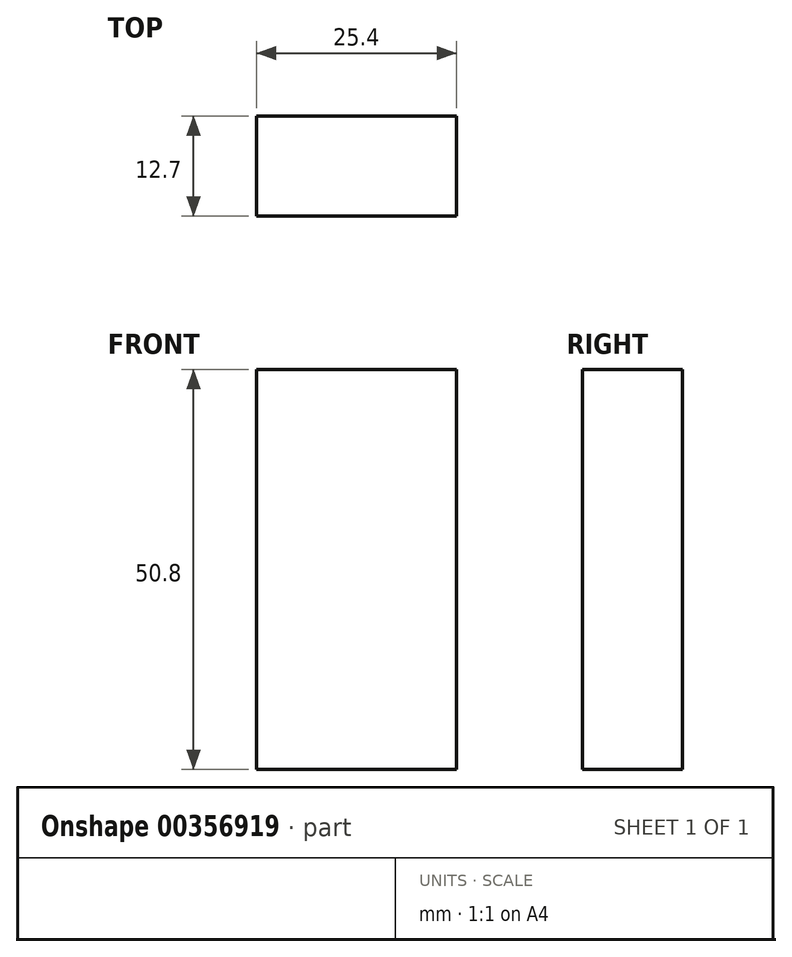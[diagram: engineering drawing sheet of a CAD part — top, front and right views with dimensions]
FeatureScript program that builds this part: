
annotation { "Feature Type Name" : "Feature", "Feature Type Description" : "" }
export const myFeature = defineFeature(function(context is Context, id is Id, definition is map)
    precondition{}
    {
        {
            var Q0;
            Q0=qCreatedBy(makeId("Right.planeOp"),FACE);
            var sketch = newSketch(context, id + "F0", { "sketchPlane" : qUnion([Q0])});
            skLineSegment(sketch, "E0.bottom", {"start": v(0, 0) * mm, "end": v(12.7, 0) * mm});
            skLineSegment(sketch, "E0.top", {"start": v(0, -50.8) * mm, "end": v(12.7, -50.8) * mm});
            skLineSegment(sketch, "E0.left", {"start": v(0, 0) * mm, "end": v(0, -50.8) * mm});
            skLineSegment(sketch, "E0.right", {"start": v(12.7, 0) * mm, "end": v(12.7, -50.8) * mm});
            skSolve(sketch);
        }
        {
            var Q0;
            Q0 = qSketchRegion(id + "F0", true);
            extrude(context, id + "F1", {"entities" : qUnion([Q0]), "depth" : 25.4 * mm});
        }
    });
